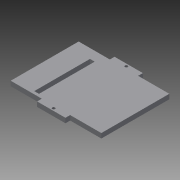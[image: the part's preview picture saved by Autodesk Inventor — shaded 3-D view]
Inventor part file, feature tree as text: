
AUTODESK INVENTOR PART (.ipt)
format: ipt  version: 2014 (Build 180170000, 170)  size: 94,208 bytes
history: native  units: mm
features: reference x3, extrude x1, sketch x1
ambient origin geometry x8: Origin, YZ Plane, XZ Plane, XY Plane, X Axis, Y Axis, Z Axis, Center Point
bodies: 实体1 (feature_tree)
feature tree (5):
  extrude  "拉伸1"  Depth=10.0mm
  sketch  "草图1"  dims[d0=3.0mm d1=10.0mm d2=59.0mm d3=5.0mm d4=22.0mm d6=3.0mm d7=3.0mm d8=5.0mm d9=0.0mm]
  reference  "参考1"
  reference  "参考2"
  reference  "参考3"
